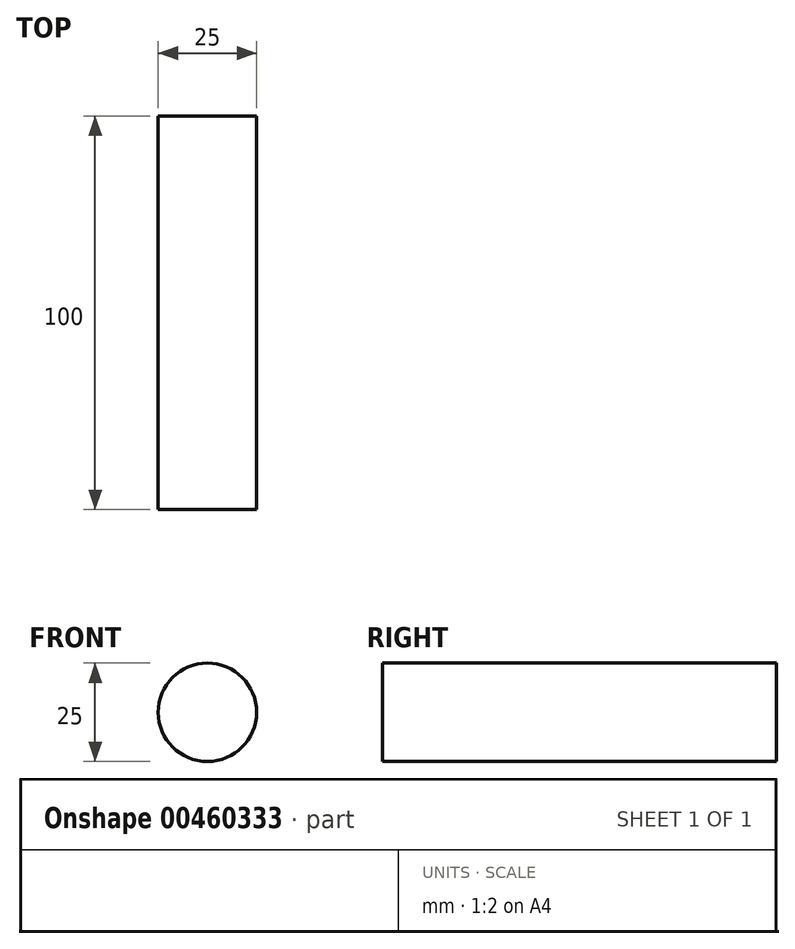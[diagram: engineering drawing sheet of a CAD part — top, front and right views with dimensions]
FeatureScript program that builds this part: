
annotation { "Feature Type Name" : "Feature", "Feature Type Description" : "" }
export const myFeature = defineFeature(function(context is Context, id is Id, definition is map)
    precondition{}
    {
        {
            var Q0;
            Q0=qCreatedBy(makeId("Front.planeOp"),FACE);
            var sketch = newSketch(context, id + "F0", { "sketchPlane" : qUnion([Q0])});
            skCircle(sketch, "E0", {"center": v(-32.6, 29.96) * mm, "radius": 12.5 * mm});
            skSolve(sketch);
        }
        {
            var Q0;
            Q0 = qSketchRegion(id + "F0", true);
            extrude(context, id + "F1", {"entities" : qUnion([Q0]), "depth" : 100 * mm});
        }
    });
